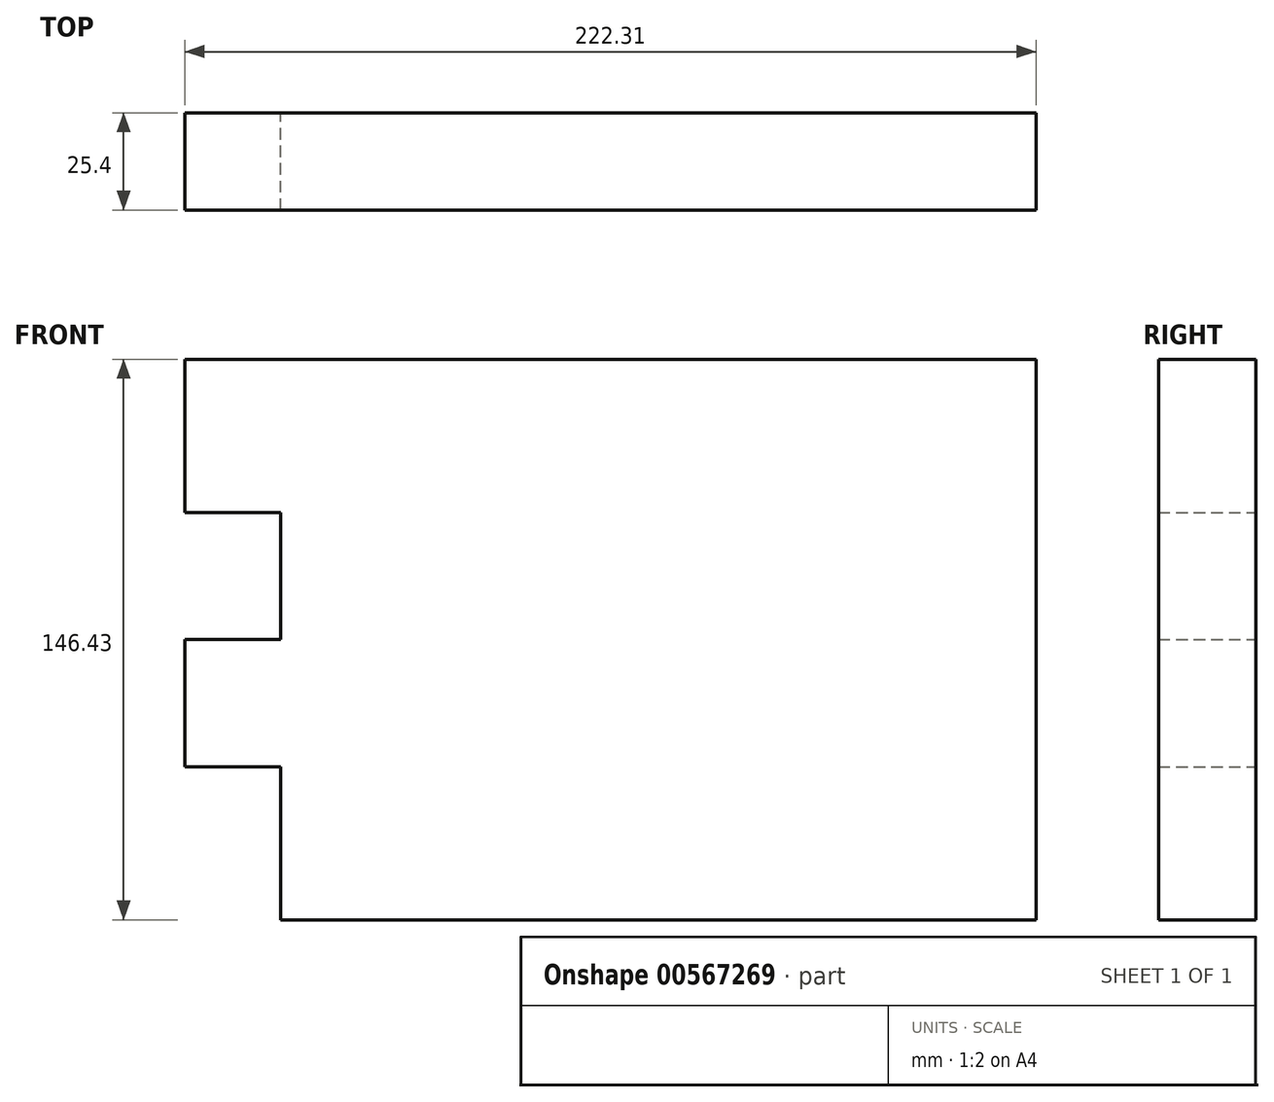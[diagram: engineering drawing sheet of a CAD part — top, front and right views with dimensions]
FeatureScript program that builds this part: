
annotation { "Feature Type Name" : "Feature", "Feature Type Description" : "" }
export const myFeature = defineFeature(function(context is Context, id is Id, definition is map)
    precondition{}
    {
        {
            var Q0;
            Q0=qCreatedBy(makeId("Front.planeOp"),FACE);
            var sketch = newSketch(context, id + "F0", { "sketchPlane" : qUnion([Q0])});
            skLineSegment(sketch, "E0.bottom", {"start": v(0, 0) * mm, "end": v(-197.35, 0) * mm});
            skLineSegment(sketch, "E0.top", {"start": v(0, 146.43) * mm, "end": v(-222.31, 146.43) * mm});
            skLineSegment(sketch, "E0.left", {"start": v(0, 0) * mm, "end": v(0, 146.43) * mm});
            skLineSegment(sketch, "E0.right", {"start": v(-222.31, 40) * mm, "end": v(-222.31, 73.22) * mm});
            skLineSegment(sketch, "E1", {"start": v(-197.35, 146.43) * mm, "end": v(-197.35, 0) * mm});
            skLineSegment(sketch, "E2", {"start": v(-197.35, 106.43) * mm, "end": v(-222.31, 106.43) * mm});
            skLineSegment(sketch, "E3", {"start": v(-197.35, 73.22) * mm, "end": v(-222.31, 73.22) * mm});
            skLineSegment(sketch, "E4", {"start": v(-197.35, 40) * mm, "end": v(-222.31, 40) * mm});
            skLineSegment(sketch, "E5.trimOffspring", {"start": v(-222.31, 106.43) * mm, "end": v(-222.31, 146.43) * mm});
            skPoint(sketch, "E6.orphan", {"position": v(-222.31, 0) * mm});
            skSolve(sketch);
        }
        {
            var Q0;
            Q0 = qSketchRegion(id + "F0", true);
            extrude(context, id + "F1", {"entities" : qUnion([Q0]), "depth" : 25.4 * mm, "offsetDistance" : 25.4 * mm});
        }
    });
